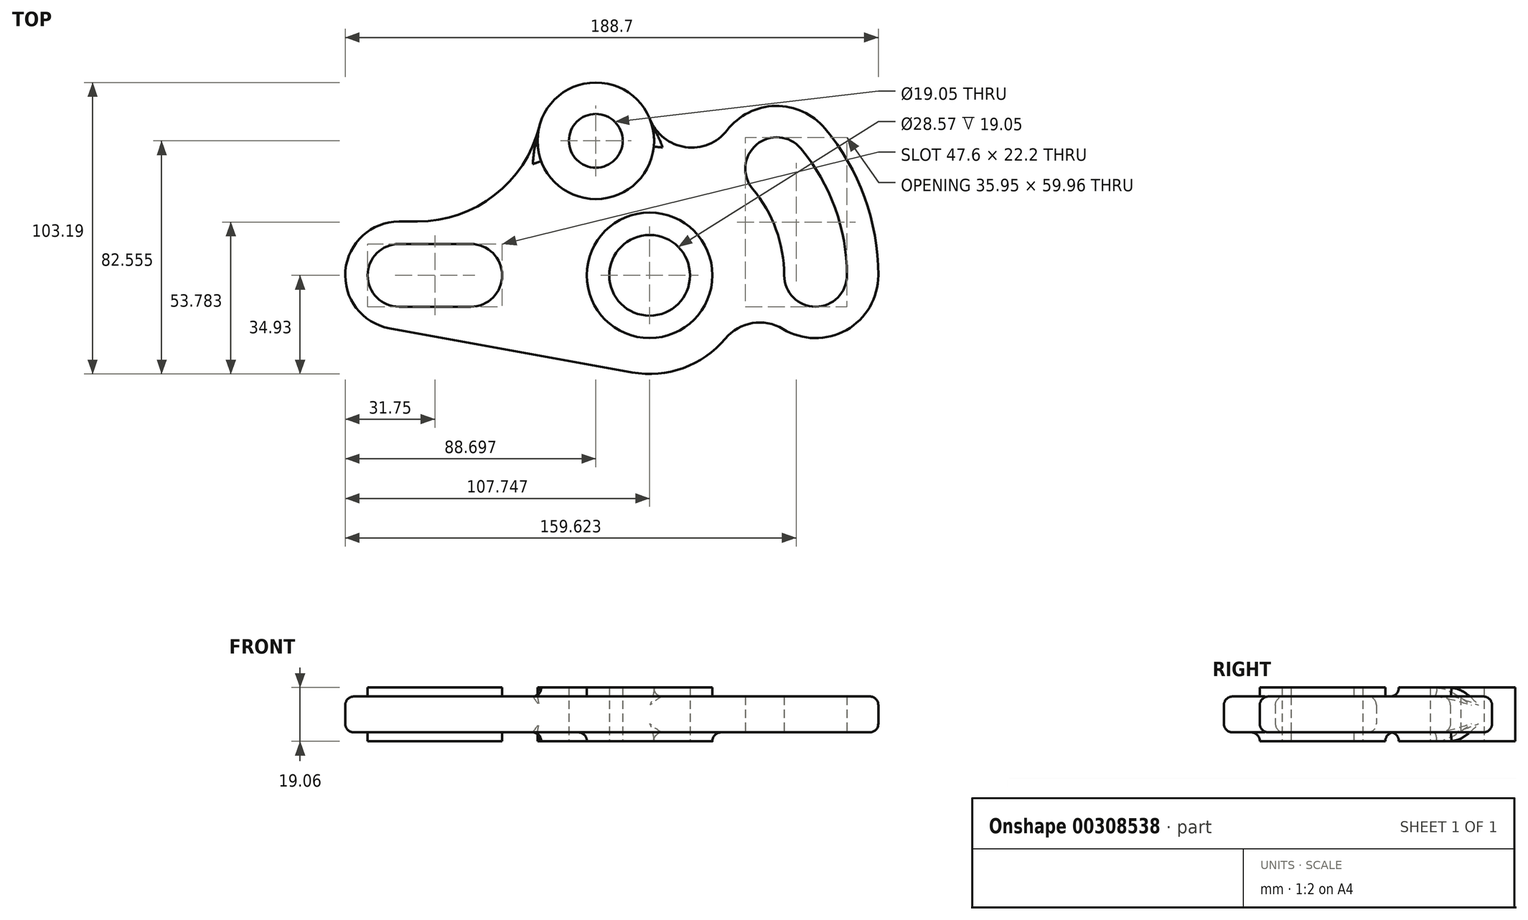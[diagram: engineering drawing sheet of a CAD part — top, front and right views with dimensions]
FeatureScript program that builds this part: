
annotation { "Feature Type Name" : "Feature", "Feature Type Description" : "" }
export const myFeature = defineFeature(function(context is Context, id is Id, definition is map)
    precondition{}
    {
        {
            var Q0;
            Q0=qCreatedBy(makeId("Top.planeOp"),FACE);
            var sketch = newSketch(context, id + "F0", { "sketchPlane" : qUnion([Q0])});
            skLineSegment(sketch, "E0", {"start": v(0, 0) * mm, "end": v(25.4, 0) * mm, "construction": true});
            skCircle(sketch, "E1", {"center": v(69.65, 47.63) * mm, "radius": 9.53 * mm});
            skCircle(sketch, "E2", {"center": v(69.65, 47.63) * mm, "radius": 20.64 * mm});
            skCircle(sketch, "E3", {"center": v(88.7, 0) * mm, "radius": 14.29 * mm});
            skCircle(sketch, "E4", {"center": v(88.7, 0) * mm, "radius": 22.23 * mm});
            skArc(sketch, "E5", {"start": v(147.42, 0) * mm, "mid": v(143.88, 20.09) * mm, "end": v(133.68, 37.75) * mm, "construction": true});
            skLineSegment(sketch, "E6", {"start": v(88.7, 0) * mm, "end": v(147.42, 0) * mm, "construction": true});
            skLineSegment(sketch, "E7", {"start": v(88.7, 0) * mm, "end": v(133.68, 37.75) * mm, "construction": true});
            skArc(sketch, "E8", {"start": v(82.45, -34.36) * mm, "mid": v(100.58, -32.84) * mm, "end": v(115.5, -22.4) * mm});
            skArc(sketch, "E9.0.startCap", {"start": v(0, -11.1) * mm, "mid": v(-11.1, 0) * mm, "end": v(0, 11.1) * mm});
            skArc(sketch, "E9.0.endCap", {"start": v(25.4, 11.1) * mm, "mid": v(36.5, 0) * mm, "end": v(25.4, -11.1) * mm});
            skLineSegment(sketch, "E9.0.left", {"start": v(0, 11.1) * mm, "end": v(25.4, 11.1) * mm});
            skLineSegment(sketch, "E9.0.right", {"start": v(0, -11.1) * mm, "end": v(25.4, -11.1) * mm});
            skArc(sketch, "E10.0.startCap", {"start": v(0, -19.05) * mm, "mid": v(-19.05, 0) * mm, "end": v(0, 19.05) * mm});
            skArc(sketch, "E10.0.endCap", {"start": v(25.4, 19.05) * mm, "mid": v(44.45, 0) * mm, "end": v(25.4, -19.05) * mm});
            skLineSegment(sketch, "E10.0.left", {"start": v(0, 19.05) * mm, "end": v(25.4, 19.05) * mm});
            skLineSegment(sketch, "E10.0.right", {"start": v(0, -19.05) * mm, "end": v(25.4, -19.05) * mm});
            skArc(sketch, "E11.0.startCap", {"start": v(158.55, 0) * mm, "mid": v(147.42, -11.13) * mm, "end": v(136.3, 0) * mm});
            skArc(sketch, "E11.0.endCap", {"start": v(125.16, 30.6) * mm, "mid": v(126.53, 46.27) * mm, "end": v(142.2, 44.9) * mm});
            skArc(sketch, "E11.0.left", {"start": v(136.3, 0) * mm, "mid": v(133.43, 16.28) * mm, "end": v(125.16, 30.6) * mm});
            skArc(sketch, "E11.0.right", {"start": v(158.55, 0) * mm, "mid": v(154.33, 23.9) * mm, "end": v(142.2, 44.9) * mm});
            skArc(sketch, "E12.0.startCap", {"start": v(169.65, 0) * mm, "mid": v(147.42, -22.22) * mm, "end": v(125.2, 0) * mm});
            skArc(sketch, "E12.0.endCap", {"start": v(116.66, 23.46) * mm, "mid": v(119.4, 54.77) * mm, "end": v(150.7, 52.03) * mm});
            skArc(sketch, "E12.0.left", {"start": v(125.2, 0) * mm, "mid": v(123, 12.48) * mm, "end": v(116.66, 23.46) * mm});
            skArc(sketch, "E12.0.right", {"start": v(169.65, 0) * mm, "mid": v(164.76, 27.69) * mm, "end": v(150.7, 52.03) * mm});
            skLineSegment(sketch, "E13", {"start": v(82.45, -34.36) * mm, "end": v(-3.4, -18.74) * mm});
            skArc(sketch, "E14", {"start": v(49.63, 52.66) * mm, "mid": v(33.86, 28.45) * mm, "end": v(6.52, 19.05) * mm});
            skArc(sketch, "E15", {"start": v(135.9, -19) * mm, "mid": v(125.07, -16.92) * mm, "end": v(115.5, -22.4) * mm});
            skArc(sketch, "E16", {"start": v(88.83, 55.24) * mm, "mid": v(101.35, 45.39) * mm, "end": v(116.12, 51.37) * mm});
            skSolve(sketch);
        }
        {
            var Q0;
            Q0=qSketchRegion(id+"F0",true);
            extrude(context, id + "F1", {"entities" : qUnion([Q0]), "endBound" : BoundingType.SYMMETRIC, "depth" : 12.7 * mm});
        }
        {
            var Q0;
            Q0=makeQuery(id+"F0.imprint","IMPRINT",FACE,{"disambiguationData":[TD([[makeQuery(id+"F0.imprint","IMPRINT",EDGE,{"derivedFrom":sQuery(id+"F0.wireOp",EDGE,"E9.0.startCap")}),1.0]])]});
            var Q1;
            Q1=makeQuery(id+"F0.imprint","IMPRINT",FACE,{"disambiguationData":[TD([[makeQuery(id+"F0.imprint","IMPRINT",EDGE,{"derivedFrom":sQuery(id+"F0.wireOp",EDGE,"E3")}),-1.0]])]});
            var Q2;
            Q2=makeQuery(id+"F0.imprint","IMPRINT",FACE,{"disambiguationData":[TD([[makeQuery(id+"F0.imprint","IMPRINT",EDGE,{"derivedFrom":sQuery(id+"F0.wireOp",EDGE,"E1")}),-1.0]])]});
            extrude(context, id + "F2", {"entities" : qUnion([Q0, Q1, Q2]), "operationType" : NewBodyOperationType.ADD, "endBound" : BoundingType.SYMMETRIC, "depth" : 19.05 * mm});
        }
        {
            var Q0;
            Q0=makeQuery(id+"F1.opExtrude","CAP_EDGE",EDGE,{"disambiguationData":[OSD([sQuery(id+"F0.wireOp",EDGE,"E15")])],"isStart":false});
            var Q1;
            Q1=makeQuery(id+"F1.opExtrude","CAP_EDGE",EDGE,{"disambiguationData":[OSD([sQuery(id+"F0.wireOp",EDGE,"E4")])],"isStart":false});
            var Q2;
            Q2=makeQuery(id+"F2.boolean.opBoolean","INTERSECT",EDGE,{"derivedFrom":[makeQuery(id+"F1.opExtrude","CAP_FACE",FACE,{"disambiguationData":[OSD([sQuery(id+"F0.wireOp",EDGE,"E1"),sQuery(id+"F0.wireOp",EDGE,"E2"),sQuery(id+"F0.wireOp",EDGE,"E4"),sQuery(id+"F0.wireOp",EDGE,"E8"),sQuery(id+"F0.wireOp",EDGE,"E9.0.startCap"),sQuery(id+"F0.wireOp",EDGE,"E9.0.endCap"),sQuery(id+"F0.wireOp",EDGE,"E9.0.left"),sQuery(id+"F0.wireOp",EDGE,"E9.0.right"),sQuery(id+"F0.wireOp",EDGE,"E10.0.startCap"),sQuery(id+"F0.wireOp",EDGE,"E10.0.left"),sQuery(id+"F0.wireOp",EDGE,"E11.0.startCap"),sQuery(id+"F0.wireOp",EDGE,"E11.0.endCap"),sQuery(id+"F0.wireOp",EDGE,"E11.0.left"),sQuery(id+"F0.wireOp",EDGE,"E11.0.right"),sQuery(id+"F0.wireOp",EDGE,"E12.0.startCap"),sQuery(id+"F0.wireOp",EDGE,"E12.0.endCap"),sQuery(id+"F0.wireOp",EDGE,"E12.0.right"),sQuery(id+"F0.wireOp",EDGE,"E13"),sQuery(id+"F0.wireOp",EDGE,"E14"),sQuery(id+"F0.wireOp",EDGE,"E15"),sQuery(id+"F0.wireOp",EDGE,"E16")])],"isStart":false}),makeQuery(id+"F2.opExtrude","SWEPT_FACE",FACE,{"disambiguationData":[OSD([sQuery(id+"F0.wireOp",EDGE,"E10.0.endCap")])]})]});
            var Q3;
            {var subQ0=sQuery(id+"F0.wireOp",EDGE,"E2");Q3=makeQuery(id+"F2.boolean.opBoolean","INTERSECT",EDGE,{"derivedFrom":[makeQuery(id+"F1.opExtrude","CAP_FACE",FACE,{"disambiguationData":[OSD([sQuery(id+"F0.wireOp",EDGE,"E1"),subQ0,sQuery(id+"F0.wireOp",EDGE,"E4"),sQuery(id+"F0.wireOp",EDGE,"E8"),sQuery(id+"F0.wireOp",EDGE,"E9.0.startCap"),sQuery(id+"F0.wireOp",EDGE,"E9.0.endCap"),sQuery(id+"F0.wireOp",EDGE,"E9.0.left"),sQuery(id+"F0.wireOp",EDGE,"E9.0.right"),sQuery(id+"F0.wireOp",EDGE,"E10.0.startCap"),sQuery(id+"F0.wireOp",EDGE,"E10.0.left"),sQuery(id+"F0.wireOp",EDGE,"E11.0.startCap"),sQuery(id+"F0.wireOp",EDGE,"E11.0.endCap"),sQuery(id+"F0.wireOp",EDGE,"E11.0.left"),sQuery(id+"F0.wireOp",EDGE,"E11.0.right"),sQuery(id+"F0.wireOp",EDGE,"E12.0.startCap"),sQuery(id+"F0.wireOp",EDGE,"E12.0.endCap"),sQuery(id+"F0.wireOp",EDGE,"E12.0.right"),sQuery(id+"F0.wireOp",EDGE,"E13"),sQuery(id+"F0.wireOp",EDGE,"E14"),sQuery(id+"F0.wireOp",EDGE,"E15"),sQuery(id+"F0.wireOp",EDGE,"E16")])],"isStart":false}),makeQuery(id+"F2.opExtrude","SWEPT_FACE",FACE,{"disambiguationData":[OSD([subQ0])]})]});}
            var Q4;
            Q4=makeQuery(id+"F2.boolean.opBoolean","INTERSECT",EDGE,{"derivedFrom":[makeQuery(id+"F1.opExtrude","CAP_FACE",FACE,{"disambiguationData":[OSD([sQuery(id+"F0.wireOp",EDGE,"E1"),sQuery(id+"F0.wireOp",EDGE,"E2"),sQuery(id+"F0.wireOp",EDGE,"E4"),sQuery(id+"F0.wireOp",EDGE,"E8"),sQuery(id+"F0.wireOp",EDGE,"E9.0.startCap"),sQuery(id+"F0.wireOp",EDGE,"E9.0.endCap"),sQuery(id+"F0.wireOp",EDGE,"E9.0.left"),sQuery(id+"F0.wireOp",EDGE,"E9.0.right"),sQuery(id+"F0.wireOp",EDGE,"E10.0.startCap"),sQuery(id+"F0.wireOp",EDGE,"E10.0.left"),sQuery(id+"F0.wireOp",EDGE,"E11.0.startCap"),sQuery(id+"F0.wireOp",EDGE,"E11.0.endCap"),sQuery(id+"F0.wireOp",EDGE,"E11.0.left"),sQuery(id+"F0.wireOp",EDGE,"E11.0.right"),sQuery(id+"F0.wireOp",EDGE,"E12.0.startCap"),sQuery(id+"F0.wireOp",EDGE,"E12.0.endCap"),sQuery(id+"F0.wireOp",EDGE,"E12.0.right"),sQuery(id+"F0.wireOp",EDGE,"E13"),sQuery(id+"F0.wireOp",EDGE,"E14"),sQuery(id+"F0.wireOp",EDGE,"E15"),sQuery(id+"F0.wireOp",EDGE,"E16")])],"isStart":true}),makeQuery(id+"F2.opExtrude","SWEPT_FACE",FACE,{"disambiguationData":[OSD([sQuery(id+"F0.wireOp",EDGE,"E10.0.endCap")])]})]});
            var Q5;
            Q5=makeQuery(id+"F1.opExtrude","CAP_EDGE",EDGE,{"disambiguationData":[OSD([sQuery(id+"F0.wireOp",EDGE,"E4")])],"isStart":true});
            var Q6;
            {var subQ0=sQuery(id+"F0.wireOp",EDGE,"E2");Q6=makeQuery(id+"F2.boolean.opBoolean","INTERSECT",EDGE,{"derivedFrom":[makeQuery(id+"F1.opExtrude","CAP_FACE",FACE,{"disambiguationData":[OSD([sQuery(id+"F0.wireOp",EDGE,"E1"),subQ0,sQuery(id+"F0.wireOp",EDGE,"E4"),sQuery(id+"F0.wireOp",EDGE,"E8"),sQuery(id+"F0.wireOp",EDGE,"E9.0.startCap"),sQuery(id+"F0.wireOp",EDGE,"E9.0.endCap"),sQuery(id+"F0.wireOp",EDGE,"E9.0.left"),sQuery(id+"F0.wireOp",EDGE,"E9.0.right"),sQuery(id+"F0.wireOp",EDGE,"E10.0.startCap"),sQuery(id+"F0.wireOp",EDGE,"E10.0.left"),sQuery(id+"F0.wireOp",EDGE,"E11.0.startCap"),sQuery(id+"F0.wireOp",EDGE,"E11.0.endCap"),sQuery(id+"F0.wireOp",EDGE,"E11.0.left"),sQuery(id+"F0.wireOp",EDGE,"E11.0.right"),sQuery(id+"F0.wireOp",EDGE,"E12.0.startCap"),sQuery(id+"F0.wireOp",EDGE,"E12.0.endCap"),sQuery(id+"F0.wireOp",EDGE,"E12.0.right"),sQuery(id+"F0.wireOp",EDGE,"E13"),sQuery(id+"F0.wireOp",EDGE,"E14"),sQuery(id+"F0.wireOp",EDGE,"E15"),sQuery(id+"F0.wireOp",EDGE,"E16")])],"isStart":true}),makeQuery(id+"F2.opExtrude","SWEPT_FACE",FACE,{"disambiguationData":[OSD([subQ0])]})]});}
            var Q7;
            Q7=makeQuery(id+"F1.opExtrude","CAP_EDGE",EDGE,{"disambiguationData":[OSD([sQuery(id+"F0.wireOp",EDGE,"E12.0.endCap")])],"isStart":true});
            var Q8;
            Q8=makeQuery(id+"F1.opExtrude","CAP_EDGE",EDGE,{"disambiguationData":[OSD([sQuery(id+"F0.wireOp",EDGE,"E14")])],"isStart":true});
            var Q9;
            Q9=makeQuery(id+"F1.opExtrude","CAP_EDGE",EDGE,{"disambiguationData":[OSD([sQuery(id+"F0.wireOp",EDGE,"E14")])],"isStart":false});
            fillet(context, id + "F3", {"entities" : qUnion([Q0, Q1, Q2, Q3, Q4, Q5, Q6, Q7, Q8, Q9]), "radius" : 3.05 * mm, "tangentPropagation" : true, "allowEdgeOverflow" : false});
        }
    });
